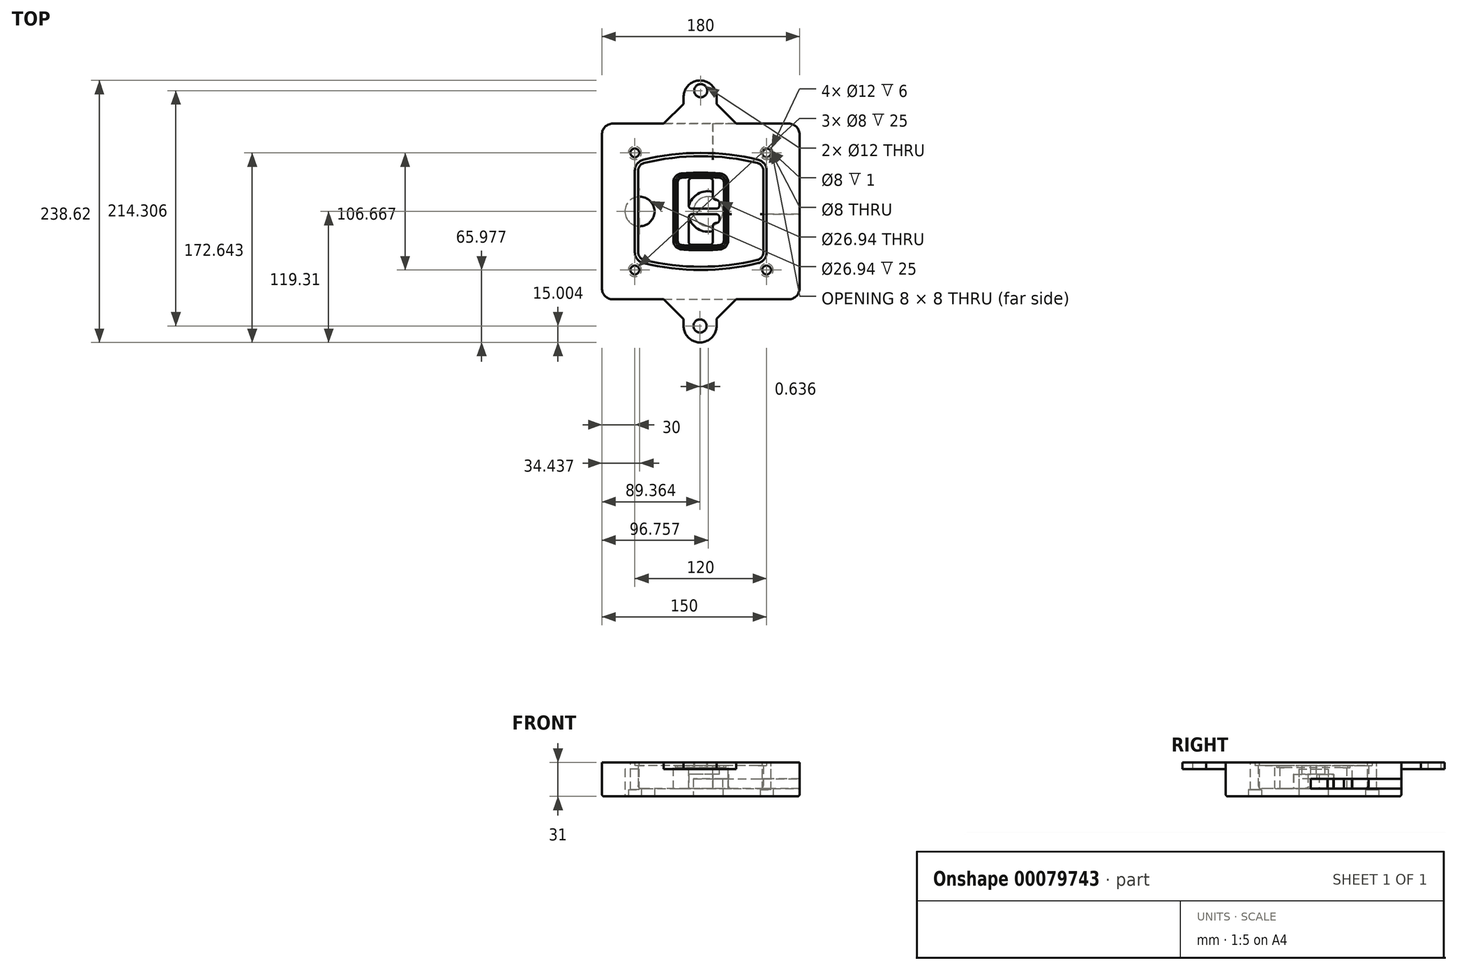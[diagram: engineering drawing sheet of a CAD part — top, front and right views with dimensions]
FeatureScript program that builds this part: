
annotation { "Feature Type Name" : "Feature", "Feature Type Description" : "" }
export const myFeature = defineFeature(function(context is Context, id is Id, definition is map)
    precondition{}
    {
        {
            var Q0;
            Q0=qCreatedBy(makeId("Top.planeOp"),FACE);
            var sketch = newSketch(context, id + "F0", { "sketchPlane" : qUnion([Q0])});
            skPoint(sketch, "E0.rect.middle", {"position": v(0, 0) * mm});
            skLineSegment(sketch, "E1.bottom", {"start": v(-80, -80) * mm, "end": v(80, -80) * mm});
            skLineSegment(sketch, "E1.top", {"start": v(-80, 80) * mm, "end": v(80, 80) * mm});
            skLineSegment(sketch, "E1.left", {"start": v(-90, -70) * mm, "end": v(-90, 70) * mm});
            skLineSegment(sketch, "E1.right", {"start": v(90, -70) * mm, "end": v(90, 70) * mm});
            skLineSegment(sketch, "E2", {"start": v(-90, 80) * mm, "end": v(90, -80) * mm, "construction": true});
            skLineSegment(sketch, "E3", {"start": v(90, 80) * mm, "end": v(-90, -80) * mm, "construction": true});
            skCircle(sketch, "E4", {"center": v(-60, 53.33) * mm, "radius": 4 * mm});
            skCircle(sketch, "E5", {"center": v(60, 53.33) * mm, "radius": 4 * mm});
            skCircle(sketch, "E6", {"center": v(60, -53.33) * mm, "radius": 4 * mm});
            skCircle(sketch, "E7", {"center": v(-60, -53.33) * mm, "radius": 4 * mm});
            skLineSegment(sketch, "E8", {"start": v(-60, 53.33) * mm, "end": v(60, 53.33) * mm, "construction": true});
            skLineSegment(sketch, "E9", {"start": v(60, 53.33) * mm, "end": v(60, -53.33) * mm, "construction": true});
            skLineSegment(sketch, "E10", {"start": v(60, -53.33) * mm, "end": v(-60, -53.33) * mm, "construction": true});
            skLineSegment(sketch, "E11", {"start": v(-60, -53.33) * mm, "end": v(-60, 53.33) * mm, "construction": true});
            skLineSegment(sketch, "E12", {"start": v(-60, 37.3) * mm, "end": v(-60, -37.3) * mm});
            skLineSegment(sketch, "E13", {"start": v(60, 37.3) * mm, "end": v(60, -37.3) * mm});
            skArc(sketch, "E14", {"start": v(52.38, 47.01) * mm, "mid": v(0, 53.33) * mm, "end": v(-52.38, 47.01) * mm});
            skArc(sketch, "E15", {"start": v(-52.38, -47.01) * mm, "mid": v(0, -53.33) * mm, "end": v(52.38, -47.01) * mm});
            skLineSegment(sketch, "E16", {"start": v(-60, 0) * mm, "end": v(60, 0) * mm, "construction": true});
            skPoint(sketch, "E17.visualSharp", {"position": v(-60, -45) * mm});
            skArc(sketch, "E17.filletArc", {"start": v(-60, -37.3) * mm, "mid": v(-57.87, -43.47) * mm, "end": v(-52.38, -47.01) * mm});
            skPoint(sketch, "E18.visualSharp", {"position": v(-60, 45) * mm});
            skArc(sketch, "E18.filletArc", {"start": v(-52.38, 47.01) * mm, "mid": v(-57.87, 43.47) * mm, "end": v(-60, 37.3) * mm});
            skPoint(sketch, "E19.visualSharp", {"position": v(60, 45) * mm});
            skArc(sketch, "E19.filletArc", {"start": v(60, 37.3) * mm, "mid": v(57.87, 43.47) * mm, "end": v(52.38, 47.01) * mm});
            skPoint(sketch, "E20.visualSharp", {"position": v(60, -45) * mm});
            skArc(sketch, "E20.filletArc", {"start": v(52.38, -47.01) * mm, "mid": v(57.87, -43.47) * mm, "end": v(60, -37.3) * mm});
            skPoint(sketch, "E21.visualSharp", {"position": v(-90, 80) * mm});
            skArc(sketch, "E21.filletArc", {"start": v(-80, 80) * mm, "mid": v(-87.07, 77.07) * mm, "end": v(-90, 70) * mm});
            skPoint(sketch, "E22.visualSharp", {"position": v(90, 80) * mm});
            skArc(sketch, "E22.filletArc", {"start": v(90, 70) * mm, "mid": v(87.07, 77.07) * mm, "end": v(80, 80) * mm});
            skPoint(sketch, "E23.visualSharp", {"position": v(90, -80) * mm});
            skArc(sketch, "E23.filletArc", {"start": v(80, -80) * mm, "mid": v(87.07, -77.07) * mm, "end": v(90, -70) * mm});
            skPoint(sketch, "E24.visualSharp", {"position": v(-90, -80) * mm});
            skArc(sketch, "E24.filletArc", {"start": v(-90, -70) * mm, "mid": v(-87.07, -77.07) * mm, "end": v(-80, -80) * mm});
            skArc(sketch, "E25.0", {"start": v(57, 37.3) * mm, "mid": v(55.5, 41.62) * mm, "end": v(51.67, 44.1) * mm});
            skLineSegment(sketch, "E25.1", {"start": v(57, 37.3) * mm, "end": v(57, -37.3) * mm});
            skArc(sketch, "E25.2", {"start": v(51.67, -44.1) * mm, "mid": v(55.5, -41.62) * mm, "end": v(57, -37.3) * mm});
            skArc(sketch, "E25.3", {"start": v(-51.67, -44.1) * mm, "mid": v(0, -50.33) * mm, "end": v(51.67, -44.1) * mm});
            skArc(sketch, "E25.4", {"start": v(-57, -37.3) * mm, "mid": v(-55.5, -41.62) * mm, "end": v(-51.67, -44.1) * mm});
            skArc(sketch, "E25.5", {"start": v(51.67, 44.1) * mm, "mid": v(0, 50.33) * mm, "end": v(-51.67, 44.1) * mm});
            skLineSegment(sketch, "E25.6", {"start": v(-57, 37.3) * mm, "end": v(-57, -37.3) * mm});
            skArc(sketch, "E25.7", {"start": v(-51.67, 44.1) * mm, "mid": v(-55.5, 41.62) * mm, "end": v(-57, 37.3) * mm});
            skArc(sketch, "E26.0", {"start": v(-53.33, 50.9) * mm, "mid": v(-61.01, 45.94) * mm, "end": v(-64, 37.3) * mm});
            skArc(sketch, "E26.1", {"start": v(53.33, 50.9) * mm, "mid": v(0, 57.33) * mm, "end": v(-53.33, 50.9) * mm});
            skArc(sketch, "E26.2", {"start": v(64, 37.3) * mm, "mid": v(61.01, 45.94) * mm, "end": v(53.33, 50.9) * mm});
            skLineSegment(sketch, "E26.3", {"start": v(64, 37.3) * mm, "end": v(64, -37.3) * mm});
            skArc(sketch, "E26.4", {"start": v(53.33, -50.9) * mm, "mid": v(61.01, -45.94) * mm, "end": v(64, -37.3) * mm});
            skLineSegment(sketch, "E26.5", {"start": v(-64, 37.3) * mm, "end": v(-64, -37.3) * mm});
            skArc(sketch, "E26.6", {"start": v(-53.33, -50.9) * mm, "mid": v(0, -57.33) * mm, "end": v(53.33, -50.9) * mm});
            skArc(sketch, "E26.7", {"start": v(-64, -37.3) * mm, "mid": v(-61.01, -45.94) * mm, "end": v(-53.33, -50.9) * mm});
            skSolve(sketch);
        }
        {
            var Q0;
            Q0=makeQuery(id+"F0.imprint","IMPRINT",FACE,{"disambiguationData":[TD([[makeQuery(id+"F0.imprint","IMPRINT",EDGE,{"derivedFrom":sQuery(id+"F0.wireOp",EDGE,"E1.bottom")}),1.0]])]});
            var Q1;
            Q1=makeQuery(id+"F0.imprint","IMPRINT",FACE,{"disambiguationData":[TD([[makeQuery(id+"F0.imprint","IMPRINT",EDGE,{"derivedFrom":sQuery(id+"F0.wireOp",EDGE,"E12")}),1.0]])]});
            var Q2;
            Q2=makeQuery(id+"F0.imprint","IMPRINT",FACE,{"disambiguationData":[TD([[makeQuery(id+"F0.imprint","IMPRINT",EDGE,{"derivedFrom":sQuery(id+"F0.wireOp",EDGE,"E25.0")}),1.0]])]});
            var Q3;
            Q3=makeQuery(id+"F0.imprint","IMPRINT",FACE,{"disambiguationData":[TD([[makeQuery(id+"F0.imprint","IMPRINT",EDGE,{"derivedFrom":sQuery(id+"F0.wireOp",EDGE,"E12")}),-1.0]])]});
            extrude(context, id + "F1", {"entities" : qUnion([Q0, Q1, Q2, Q3]), "oppositeDirection" : true, "depth" : 25 * mm});
        }
        {
            var Q0;
            Q0=makeQuery(id+"F0.imprint","IMPRINT",FACE,{"disambiguationData":[TD([[makeQuery(id+"F0.imprint","IMPRINT",EDGE,{"derivedFrom":sQuery(id+"F0.wireOp",EDGE,"E12")}),1.0]])]});
            extrude(context, id + "F2", {"entities" : qUnion([Q0]), "operationType" : NewBodyOperationType.ADD, "depth" : 3 * mm});
        }
        {
            var Q0;
            Q0=makeQuery(id+"F0.imprint","IMPRINT",FACE,{"disambiguationData":[TD([[makeQuery(id+"F0.imprint","IMPRINT",EDGE,{"derivedFrom":sQuery(id+"F0.wireOp",EDGE,"E25.0")}),1.0]])]});
            extrude(context, id + "F3", {"entities" : qUnion([Q0]), "operationType" : NewBodyOperationType.REMOVE, "oppositeDirection" : true, "depth" : 18 * mm});
        }
        {
            var Q0;
            Q0=makeQuery(id+"F2.opExtrude","CAP_FACE",FACE,{"disambiguationData":[OSD([sQuery(id+"F0.wireOp",EDGE,"E12"),sQuery(id+"F0.wireOp",EDGE,"E13"),sQuery(id+"F0.wireOp",EDGE,"E14"),sQuery(id+"F0.wireOp",EDGE,"E15"),sQuery(id+"F0.wireOp",EDGE,"E17.filletArc"),sQuery(id+"F0.wireOp",EDGE,"E18.filletArc"),sQuery(id+"F0.wireOp",EDGE,"E19.filletArc"),sQuery(id+"F0.wireOp",EDGE,"E20.filletArc"),sQuery(id+"F0.wireOp",EDGE,"E25.0"),sQuery(id+"F0.wireOp",EDGE,"E25.1"),sQuery(id+"F0.wireOp",EDGE,"E25.2"),sQuery(id+"F0.wireOp",EDGE,"E25.3"),sQuery(id+"F0.wireOp",EDGE,"E25.4"),sQuery(id+"F0.wireOp",EDGE,"E25.5"),sQuery(id+"F0.wireOp",EDGE,"E25.6"),sQuery(id+"F0.wireOp",EDGE,"E25.7")])],"isStart":false});
            var sketch = newSketch(context, id + "F4", { "sketchPlane" : qUnion([Q0])});
            skArc(sketch, "E27.0", {"start": v(-17.7, -34.56) * mm, "mid": v(0, -35.33) * mm, "end": v(17.7, -34.56) * mm});
            skArc(sketch, "E28.0", {"start": v(17.7, 34.56) * mm, "mid": v(0, 35.33) * mm, "end": v(-17.7, 34.56) * mm});
            skLineSegment(sketch, "E29", {"start": v(-25, 26.59) * mm, "end": v(-25, -26.59) * mm});
            skLineSegment(sketch, "E30", {"start": v(25, 26.59) * mm, "end": v(25, -26.59) * mm});
            skLineSegment(sketch, "E31", {"start": v(-25, 33.78) * mm, "end": v(25, 33.78) * mm, "construction": true});
            skLineSegment(sketch, "E32", {"start": v(-25, -33.78) * mm, "end": v(25, -33.78) * mm, "construction": true});
            skPoint(sketch, "E33.visualSharp", {"position": v(-25, 33.78) * mm});
            skArc(sketch, "E33.filletArc", {"start": v(-17.7, 34.56) * mm, "mid": v(-22.9, 32) * mm, "end": v(-25, 26.59) * mm});
            skPoint(sketch, "E34.visualSharp", {"position": v(25, 33.78) * mm});
            skArc(sketch, "E34.filletArc", {"start": v(25, 26.59) * mm, "mid": v(22.9, 32) * mm, "end": v(17.7, 34.56) * mm});
            skPoint(sketch, "E35.visualSharp", {"position": v(25, -33.78) * mm});
            skArc(sketch, "E35.filletArc", {"start": v(17.7, -34.56) * mm, "mid": v(22.9, -32) * mm, "end": v(25, -26.59) * mm});
            skPoint(sketch, "E36.visualSharp", {"position": v(-25, -33.78) * mm});
            skArc(sketch, "E36.filletArc", {"start": v(-25, -26.59) * mm, "mid": v(-22.9, -32) * mm, "end": v(-17.7, -34.56) * mm});
            skArc(sketch, "E37.0", {"start": v(51.67, 44.1) * mm, "mid": v(0, 50.33) * mm, "end": v(-51.67, 44.1) * mm});
            skArc(sketch, "E37.1", {"start": v(-51.67, 44.1) * mm, "mid": v(-55.5, 41.62) * mm, "end": v(-57, 37.3) * mm});
            skLineSegment(sketch, "E37.2", {"start": v(-57, 37.3) * mm, "end": v(-57, -37.3) * mm});
            skArc(sketch, "E37.3", {"start": v(-57, -37.3) * mm, "mid": v(-55.5, -41.62) * mm, "end": v(-51.67, -44.1) * mm});
            skArc(sketch, "E37.4", {"start": v(-51.67, -44.1) * mm, "mid": v(0, -50.33) * mm, "end": v(51.67, -44.1) * mm});
            skArc(sketch, "E37.5", {"start": v(51.67, -44.1) * mm, "mid": v(55.5, -41.62) * mm, "end": v(57, -37.3) * mm});
            skLineSegment(sketch, "E37.6", {"start": v(57, 37.3) * mm, "end": v(57, -37.3) * mm});
            skArc(sketch, "E37.7", {"start": v(57, 37.3) * mm, "mid": v(55.5, 41.62) * mm, "end": v(51.67, 44.1) * mm});
            skLineSegment(sketch, "E38.0", {"start": v(23, 26.59) * mm, "end": v(23, -26.59) * mm});
            skArc(sketch, "E38.1", {"start": v(17.53, -32.56) * mm, "mid": v(21.42, -30.64) * mm, "end": v(23, -26.59) * mm});
            skArc(sketch, "E38.2", {"start": v(-17.53, -32.56) * mm, "mid": v(0, -33.33) * mm, "end": v(17.53, -32.56) * mm});
            skArc(sketch, "E38.3", {"start": v(-23, -26.59) * mm, "mid": v(-21.42, -30.64) * mm, "end": v(-17.53, -32.56) * mm});
            skLineSegment(sketch, "E38.4", {"start": v(-23, 26.59) * mm, "end": v(-23, -26.59) * mm});
            skArc(sketch, "E38.5", {"start": v(23, 26.59) * mm, "mid": v(21.42, 30.64) * mm, "end": v(17.53, 32.56) * mm});
            skArc(sketch, "E38.6", {"start": v(-17.53, 32.56) * mm, "mid": v(-21.42, 30.64) * mm, "end": v(-23, 26.59) * mm});
            skArc(sketch, "E38.7", {"start": v(17.53, 32.56) * mm, "mid": v(0, 33.33) * mm, "end": v(-17.53, 32.56) * mm});
            skArc(sketch, "E39.0", {"start": v(21, 26.59) * mm, "mid": v(19.95, 29.29) * mm, "end": v(17.35, 30.57) * mm});
            skLineSegment(sketch, "E39.1", {"start": v(21, 26.59) * mm, "end": v(21, -26.59) * mm});
            skArc(sketch, "E39.2", {"start": v(17.35, -30.57) * mm, "mid": v(19.95, -29.29) * mm, "end": v(21, -26.59) * mm});
            skArc(sketch, "E39.3", {"start": v(-17.35, -30.57) * mm, "mid": v(0, -31.33) * mm, "end": v(17.35, -30.57) * mm});
            skArc(sketch, "E39.4", {"start": v(-21, -26.59) * mm, "mid": v(-19.95, -29.29) * mm, "end": v(-17.35, -30.57) * mm});
            skArc(sketch, "E39.5", {"start": v(17.35, 30.57) * mm, "mid": v(0, 31.33) * mm, "end": v(-17.35, 30.57) * mm});
            skLineSegment(sketch, "E39.6", {"start": v(-21, 26.59) * mm, "end": v(-21, -26.59) * mm});
            skArc(sketch, "E39.7", {"start": v(-17.35, 30.57) * mm, "mid": v(-19.95, 29.29) * mm, "end": v(-21, 26.59) * mm});
            skLineSegment(sketch, "E40", {"start": v(-25, 0) * mm, "end": v(25, 0) * mm, "construction": true});
            skLineSegment(sketch, "E41", {"start": v(-11, 5.5) * mm, "end": v(-11, 27.5) * mm});
            skLineSegment(sketch, "E42", {"start": v(-8, 30.5) * mm, "end": v(8, 30.5) * mm});
            skLineSegment(sketch, "E43", {"start": v(11, 27.5) * mm, "end": v(11, 13.5) * mm});
            skLineSegment(sketch, "E44", {"start": v(14, 10.5) * mm, "end": v(14, 10.5) * mm});
            skLineSegment(sketch, "E45", {"start": v(17, 7.5) * mm, "end": v(17, 5.5) * mm});
            skLineSegment(sketch, "E46", {"start": v(14, 2.5) * mm, "end": v(-8, 2.5) * mm});
            skPoint(sketch, "E47.visualSharp", {"position": v(-11, 30.5) * mm});
            skArc(sketch, "E47.filletArc", {"start": v(-8, 30.5) * mm, "mid": v(-10.12, 29.62) * mm, "end": v(-11, 27.5) * mm});
            skPoint(sketch, "E48.visualSharp", {"position": v(11, 30.5) * mm});
            skArc(sketch, "E48.filletArc", {"start": v(11, 27.5) * mm, "mid": v(10.12, 29.62) * mm, "end": v(8, 30.5) * mm});
            skPoint(sketch, "E49.visualSharp", {"position": v(11, 10.5) * mm});
            skArc(sketch, "E49.filletArc", {"start": v(11, 13.5) * mm, "mid": v(11.88, 11.38) * mm, "end": v(14, 10.5) * mm});
            skPoint(sketch, "E50.visualSharp", {"position": v(17, 10.5) * mm});
            skArc(sketch, "E50.filletArc", {"start": v(17, 7.5) * mm, "mid": v(16.12, 9.62) * mm, "end": v(14, 10.5) * mm});
            skPoint(sketch, "E51.visualSharp", {"position": v(17, 2.5) * mm});
            skArc(sketch, "E51.filletArc", {"start": v(14, 2.5) * mm, "mid": v(16.12, 3.38) * mm, "end": v(17, 5.5) * mm});
            skPoint(sketch, "E52.visualSharp", {"position": v(-11, 2.5) * mm});
            skArc(sketch, "E52.filletArc", {"start": v(-11, 5.5) * mm, "mid": v(-10.12, 3.38) * mm, "end": v(-8, 2.5) * mm});
            skLineSegment(sketch, "E53.0.MirrorCS", {"start": v(14, -2.5) * mm, "end": v(-8, -2.5) * mm});
            skArc(sketch, "E54.0.MirrorCS", {"start": v(-11, -5.5) * mm, "mid": v(-10.12, -3.38) * mm, "end": v(-8, -2.5) * mm});
            skLineSegment(sketch, "E55.0.MirrorCS", {"start": v(-11, -5.5) * mm, "end": v(-11, -27.5) * mm});
            skArc(sketch, "E56.0.MirrorCS", {"start": v(-8, -30.5) * mm, "mid": v(-10.12, -29.62) * mm, "end": v(-11, -27.5) * mm});
            skLineSegment(sketch, "E57.0.MirrorCS", {"start": v(-8, -30.5) * mm, "end": v(8, -30.5) * mm});
            skArc(sketch, "E58.0.MirrorCS", {"start": v(11, -27.5) * mm, "mid": v(10.12, -29.62) * mm, "end": v(8, -30.5) * mm});
            skLineSegment(sketch, "E59.0.MirrorCS", {"start": v(11, -27.5) * mm, "end": v(11, -13.5) * mm});
            skArc(sketch, "E60.0.MirrorCS", {"start": v(11, -13.5) * mm, "mid": v(11.88, -11.38) * mm, "end": v(14, -10.5) * mm});
            skArc(sketch, "E61.0.MirrorCS", {"start": v(17, -7.5) * mm, "mid": v(16.12, -9.62) * mm, "end": v(14, -10.5) * mm});
            skLineSegment(sketch, "E62.0.MirrorCS", {"start": v(17, -7.5) * mm, "end": v(17, -5.5) * mm});
            skArc(sketch, "E63.0.MirrorCS", {"start": v(14, -2.5) * mm, "mid": v(16.12, -3.38) * mm, "end": v(17, -5.5) * mm});
            skSolve(sketch);
        }
        {
            var Q0;
            Q0=makeQuery(id+"F4.imprint","IMPRINT",FACE,{"disambiguationData":[TD([[makeQuery(id+"F4.imprint","IMPRINT",EDGE,{"derivedFrom":sQuery(id+"F4.wireOp",EDGE,"E27.0")}),1.0]])]});
            var Q1;
            Q1=makeQuery(id+"F4.imprint","IMPRINT",FACE,{"disambiguationData":[TD([[makeQuery(id+"F4.imprint","IMPRINT",EDGE,{"derivedFrom":sQuery(id+"F4.wireOp",EDGE,"E38.0")}),-1.0]])]});
            var Q2;
            Q2=makeQuery(id+"F4.imprint","IMPRINT",FACE,{"disambiguationData":[TD([[makeQuery(id+"F4.imprint","IMPRINT",EDGE,{"derivedFrom":sQuery(id+"F4.wireOp",EDGE,"E39.0")}),1.0]])]});
            extrude(context, id + "F5", {"entities" : qUnion([Q0, Q1, Q2]), "operationType" : NewBodyOperationType.ADD, "endBound" : BoundingType.UP_TO_NEXT, "oppositeDirection" : true, "depth" : 25 * mm});
        }
        {
            var Q0;
            Q0=makeQuery(id+"F4.imprint","IMPRINT",FACE,{"disambiguationData":[TD([[makeQuery(id+"F4.imprint","IMPRINT",EDGE,{"derivedFrom":sQuery(id+"F4.wireOp",EDGE,"E38.0")}),-1.0]])]});
            extrude(context, id + "F6", {"entities" : qUnion([Q0]), "operationType" : NewBodyOperationType.REMOVE, "oppositeDirection" : true, "depth" : 2 * mm});
        }
        {
            var Q0;
            Q0=makeQuery(id+"F1.opExtrude","CAP_FACE",FACE,{"disambiguationData":[OSD([sQuery(id+"F0.wireOp",EDGE,"E1.bottom"),sQuery(id+"F0.wireOp",EDGE,"E1.top"),sQuery(id+"F0.wireOp",EDGE,"E1.left"),sQuery(id+"F0.wireOp",EDGE,"E1.right"),sQuery(id+"F0.wireOp",EDGE,"E4"),sQuery(id+"F0.wireOp",EDGE,"E5"),sQuery(id+"F0.wireOp",EDGE,"E6"),sQuery(id+"F0.wireOp",EDGE,"E7"),sQuery(id+"F0.wireOp",EDGE,"E21.filletArc"),sQuery(id+"F0.wireOp",EDGE,"E22.filletArc"),sQuery(id+"F0.wireOp",EDGE,"E23.filletArc"),sQuery(id+"F0.wireOp",EDGE,"E24.filletArc")])],"isStart":false});
            var sketch = newSketch(context, id + "F7", { "sketchPlane" : qUnion([Q0])});
            skCircle(sketch, "E64", {"center": v(6.76, 0) * mm, "radius": 13.47 * mm});
            skCircle(sketch, "E65", {"center": v(-55.56, 0) * mm, "radius": 13.47 * mm});
            skLineSegment(sketch, "E66", {"start": v(90, 0) * mm, "end": v(-90, 0) * mm});
            skCircle(sketch, "E67", {"center": v(6.76, 0) * mm, "radius": 18.47 * mm});
            skCircle(sketch, "E68", {"center": v(60, -53.33) * mm, "radius": 6 * mm});
            skCircle(sketch, "E69", {"center": v(-60, -53.33) * mm, "radius": 6 * mm});
            skCircle(sketch, "E70", {"center": v(-60, 53.33) * mm, "radius": 6 * mm});
            skCircle(sketch, "E71", {"center": v(60, 53.33) * mm, "radius": 6 * mm});
            skSolve(sketch);
        }
        {
            var Q0;
            {var subQ1=sQuery(id+"F7.wireOp",EDGE,"E66");var subQ4=sQuery(id+"F7.wireOp",EDGE,"E64");var subQ6=makeQuery(id+"F7.imprint","INTERSECT",VERTEX,{"disambiguationData":[OD(0.0)],"derivedFrom":[subQ4,subQ1]});Q0=makeQuery(id+"F7.imprint","IMPRINT",FACE,{"disambiguationData":[TD([[makeQuery(id+"F7.imprint","IMPRINT",EDGE,{"disambiguationData":[TD([[subQ6,-1.0]])],"derivedFrom":subQ4}),-1.0]])]});}
            var Q1;
            {var subQ0=sQuery(id+"F7.wireOp",EDGE,"E66");var subQ1=sQuery(id+"F7.wireOp",EDGE,"E64");var subQ3=makeQuery(id+"F7.imprint","INTERSECT",VERTEX,{"disambiguationData":[OD(0.0)],"derivedFrom":[subQ1,subQ0]});Q1=makeQuery(id+"F7.imprint","IMPRINT",FACE,{"disambiguationData":[TD([[makeQuery(id+"F7.imprint","IMPRINT",EDGE,{"disambiguationData":[TD([[subQ3,-1.0]])],"derivedFrom":subQ1}),1.0]])]});}
            var Q2;
            {var subQ0=sQuery(id+"F7.wireOp",EDGE,"E66");var subQ1=sQuery(id+"F7.wireOp",EDGE,"E64");var subQ3=makeQuery(id+"F7.imprint","INTERSECT",VERTEX,{"disambiguationData":[OD(0.0)],"derivedFrom":[subQ1,subQ0]});Q2=makeQuery(id+"F7.imprint","IMPRINT",FACE,{"disambiguationData":[TD([[makeQuery(id+"F7.imprint","IMPRINT",EDGE,{"disambiguationData":[TD([[subQ3,1.0]])],"derivedFrom":subQ1}),1.0]])]});}
            var Q3;
            {var subQ1=sQuery(id+"F7.wireOp",EDGE,"E66");var subQ4=sQuery(id+"F7.wireOp",EDGE,"E64");var subQ6=makeQuery(id+"F7.imprint","INTERSECT",VERTEX,{"disambiguationData":[OD(0.0)],"derivedFrom":[subQ4,subQ1]});Q3=makeQuery(id+"F7.imprint","IMPRINT",FACE,{"disambiguationData":[TD([[makeQuery(id+"F7.imprint","IMPRINT",EDGE,{"disambiguationData":[TD([[subQ6,1.0]])],"derivedFrom":subQ4}),-1.0]])]});}
            extrude(context, id + "F8", {"entities" : qUnion([Q0, Q1, Q2, Q3]), "operationType" : NewBodyOperationType.ADD, "oppositeDirection" : true, "depth" : 20 * mm});
        }
        {
            var Q0;
            {var subQ0=sQuery(id+"F7.wireOp",EDGE,"E66");var subQ1=sQuery(id+"F7.wireOp",EDGE,"E64");var subQ3=makeQuery(id+"F7.imprint","INTERSECT",VERTEX,{"disambiguationData":[OD(0.0)],"derivedFrom":[subQ1,subQ0]});Q0=makeQuery(id+"F7.imprint","IMPRINT",FACE,{"disambiguationData":[TD([[makeQuery(id+"F7.imprint","IMPRINT",EDGE,{"disambiguationData":[TD([[subQ3,-1.0]])],"derivedFrom":subQ1}),1.0]])]});}
            var Q1;
            {var subQ0=sQuery(id+"F7.wireOp",EDGE,"E66");var subQ1=sQuery(id+"F7.wireOp",EDGE,"E64");var subQ3=makeQuery(id+"F7.imprint","INTERSECT",VERTEX,{"disambiguationData":[OD(0.0)],"derivedFrom":[subQ1,subQ0]});Q1=makeQuery(id+"F7.imprint","IMPRINT",FACE,{"disambiguationData":[TD([[makeQuery(id+"F7.imprint","IMPRINT",EDGE,{"disambiguationData":[TD([[subQ3,1.0]])],"derivedFrom":subQ1}),1.0]])]});}
            extrude(context, id + "F9", {"entities" : qUnion([Q0, Q1]), "operationType" : NewBodyOperationType.REMOVE, "oppositeDirection" : true, "depth" : 16 * mm});
        }
        {
            var Q0;
            {var subQ0=sQuery(id+"F7.wireOp",EDGE,"E66");var subQ1=sQuery(id+"F7.wireOp",EDGE,"E65");var subQ3=makeQuery(id+"F7.imprint","INTERSECT",VERTEX,{"disambiguationData":[OD(0.0)],"derivedFrom":[subQ1,subQ0]});Q0=makeQuery(id+"F7.imprint","IMPRINT",FACE,{"disambiguationData":[TD([[makeQuery(id+"F7.imprint","IMPRINT",EDGE,{"disambiguationData":[TD([[subQ3,-1.0]])],"derivedFrom":subQ1}),1.0]])]});}
            var Q1;
            {var subQ0=sQuery(id+"F7.wireOp",EDGE,"E66");var subQ1=sQuery(id+"F7.wireOp",EDGE,"E65");var subQ3=makeQuery(id+"F7.imprint","INTERSECT",VERTEX,{"disambiguationData":[OD(0.0)],"derivedFrom":[subQ1,subQ0]});Q1=makeQuery(id+"F7.imprint","IMPRINT",FACE,{"disambiguationData":[TD([[makeQuery(id+"F7.imprint","IMPRINT",EDGE,{"disambiguationData":[TD([[subQ3,1.0]])],"derivedFrom":subQ1}),1.0]])]});}
            extrude(context, id + "F10", {"entities" : qUnion([Q0, Q1]), "operationType" : NewBodyOperationType.REMOVE, "oppositeDirection" : true, "depth" : 25 * mm});
        }
        {
            var Q0;
            Q0=makeQuery(id+"F7.imprint","IMPRINT",FACE,{"disambiguationData":[TD([[makeQuery(id+"F7.imprint","IMPRINT",EDGE,{"derivedFrom":sQuery(id+"F7.wireOp",EDGE,"E68")}),1.0]])]});
            var Q1;
            Q1=makeQuery(id+"F7.imprint","IMPRINT",FACE,{"disambiguationData":[TD([[makeQuery(id+"F7.imprint","IMPRINT",EDGE,{"derivedFrom":makeQuery(id+"F1.opExtrude","CAP_EDGE",EDGE,{"disambiguationData":[OSD([sQuery(id+"F0.wireOp",EDGE,"E5")])],"isStart":false})}),-1.0]])]});
            var Q2;
            Q2=makeQuery(id+"F7.imprint","IMPRINT",FACE,{"disambiguationData":[TD([[makeQuery(id+"F7.imprint","IMPRINT",EDGE,{"derivedFrom":sQuery(id+"F7.wireOp",EDGE,"E69")}),1.0]])]});
            var Q3;
            Q3=makeQuery(id+"F7.imprint","IMPRINT",FACE,{"disambiguationData":[TD([[makeQuery(id+"F7.imprint","IMPRINT",EDGE,{"derivedFrom":makeQuery(id+"F1.opExtrude","CAP_EDGE",EDGE,{"disambiguationData":[OSD([sQuery(id+"F0.wireOp",EDGE,"E4")])],"isStart":false})}),-1.0]])]});
            var Q4;
            Q4=makeQuery(id+"F7.imprint","IMPRINT",FACE,{"disambiguationData":[TD([[makeQuery(id+"F7.imprint","IMPRINT",EDGE,{"derivedFrom":sQuery(id+"F7.wireOp",EDGE,"E70")}),1.0]])]});
            var Q5;
            Q5=makeQuery(id+"F7.imprint","IMPRINT",FACE,{"disambiguationData":[TD([[makeQuery(id+"F7.imprint","IMPRINT",EDGE,{"derivedFrom":makeQuery(id+"F1.opExtrude","CAP_EDGE",EDGE,{"disambiguationData":[OSD([sQuery(id+"F0.wireOp",EDGE,"E7")])],"isStart":false})}),-1.0]])]});
            var Q6;
            Q6=makeQuery(id+"F7.imprint","IMPRINT",FACE,{"disambiguationData":[TD([[makeQuery(id+"F7.imprint","IMPRINT",EDGE,{"derivedFrom":sQuery(id+"F7.wireOp",EDGE,"E71")}),1.0]])]});
            var Q7;
            Q7=makeQuery(id+"F7.imprint","IMPRINT",FACE,{"disambiguationData":[TD([[makeQuery(id+"F7.imprint","IMPRINT",EDGE,{"derivedFrom":makeQuery(id+"F1.opExtrude","CAP_EDGE",EDGE,{"disambiguationData":[OSD([sQuery(id+"F0.wireOp",EDGE,"E6")])],"isStart":false})}),-1.0]])]});
            extrude(context, id + "F11", {"entities" : qUnion([Q0, Q1, Q2, Q3, Q4, Q5, Q6, Q7]), "operationType" : NewBodyOperationType.REMOVE, "oppositeDirection" : true, "depth" : 6 * mm});
        }
        {
            var Q0;
            Q0=makeQuery(id+"F9.boolean.opBoolean","COPY",FACE,{"derivedFrom":makeQuery(id+"F9.opExtrude","CAP_FACE",FACE,{"disambiguationData":[OSD([sQuery(id+"F7.wireOp",EDGE,"E64")])],"isStart":false})});
            var sketch = newSketch(context, id + "F12", { "sketchPlane" : qUnion([Q0])});
            skArc(sketch, "E72.0", {"start": v(11, -88.19) * mm, "mid": v(97.1, -83.6) * mm, "end": v(92.5, 2.5) * mm});
            skLineSegment(sketch, "E72.1", {"start": v(11, -17.97) * mm, "end": v(11, -17.97) * mm});
            skLineSegment(sketch, "E73", {"start": v(92.5, -105.13) * mm, "end": v(102.3, -105.13) * mm});
            skLineSegment(sketch, "E74.0", {"start": v(92.5, 2.5) * mm, "end": v(14, 2.5) * mm});
            skArc(sketch, "E74.1", {"start": v(14, 2.5) * mm, "mid": v(16.12, 3.38) * mm, "end": v(17, 5.5) * mm});
            skLineSegment(sketch, "E74.2", {"start": v(17, 7.5) * mm, "end": v(17, 5.5) * mm});
            skArc(sketch, "E74.3", {"start": v(17, 7.5) * mm, "mid": v(16.12, 9.62) * mm, "end": v(14, 10.5) * mm});
            skArc(sketch, "E74.4", {"start": v(11, 13.5) * mm, "mid": v(11.88, 11.38) * mm, "end": v(14, 10.5) * mm});
            skLineSegment(sketch, "E74.5", {"start": v(11, 13.5) * mm, "end": v(11, -88.19) * mm});
            skLineSegment(sketch, "E74.7", {"start": v(92.5, -2.5) * mm, "end": v(14, -2.5) * mm});
            skArc(sketch, "E74.8", {"start": v(14, -2.5) * mm, "mid": v(16.12, -3.38) * mm, "end": v(17, -5.5) * mm});
            skLineSegment(sketch, "E74.9", {"start": v(17, -7.5) * mm, "end": v(17, -5.5) * mm});
            skArc(sketch, "E74.10", {"start": v(17, -7.5) * mm, "mid": v(16.12, -9.62) * mm, "end": v(14, -10.5) * mm});
            skArc(sketch, "E74.11", {"start": v(11, -13.5) * mm, "mid": v(11.88, -11.38) * mm, "end": v(14, -10.5) * mm});
            skLineSegment(sketch, "E74.12", {"start": v(11, -17.97) * mm, "end": v(11, -13.5) * mm});
            skPoint(sketch, "E75.orphan", {"position": v(11, -27.5) * mm});
            skPoint(sketch, "E76.orphan", {"position": v(-8, -2.5) * mm});
            skPoint(sketch, "E77.orphan", {"position": v(-8, 2.5) * mm});
            skPoint(sketch, "E78.orphan", {"position": v(11, 27.5) * mm});
            skSolve(sketch);
        }
        {
            var Q0;
            {var subQ7=sQuery(id+"F12.wireOp",EDGE,"E72.0");var subQ14=sQuery(id+"F12.wireOp",EDGE,"E72.1");var subQ16=sQuery(id+"F12.wireOp",EDGE,"E74.1");var subQ18=sQuery(id+"F12.wireOp",EDGE,"E74.8");Q0=qUnion([makeQuery(id+"F12.imprint","IMPRINT",FACE,{"disambiguationData":[TD([[makeQuery(id+"F12.imprint","IMPRINT",EDGE,{"derivedFrom":subQ7}),1.0]])]}),makeQuery(id+"F12.imprint","IMPRINT",FACE,{"disambiguationData":[TD([[makeQuery(id+"F12.imprint","IMPRINT",EDGE,{"derivedFrom":subQ14}),1.0]])]}),makeQuery(id+"F12.imprint","IMPRINT",FACE,{"disambiguationData":[TD([[makeQuery(id+"F12.imprint","IMPRINT",EDGE,{"derivedFrom":subQ16}),1.0]])]}),makeQuery(id+"F12.imprint","IMPRINT",FACE,{"disambiguationData":[TD([[makeQuery(id+"F12.imprint","IMPRINT",EDGE,{"derivedFrom":subQ18}),-1.0]])]})]);}
            var Q1;
            Q1=makeQuery(id+"F5.boolean.opBoolean","SPLIT",FACE,{"disambiguationData":[TD([makeQuery(id+"F5.opExtrude","SWEPT_FACE",FACE,{"disambiguationData":[OSD([sQuery(id+"F4.wireOp",EDGE,"E41")])]})])],"derivedFrom":makeQuery(id+"F3.boolean.opBoolean","COPY",FACE,{"derivedFrom":makeQuery(id+"F3.opExtrude","CAP_FACE",FACE,{"disambiguationData":[OSD([sQuery(id+"F0.wireOp",EDGE,"E25.0"),sQuery(id+"F0.wireOp",EDGE,"E25.1"),sQuery(id+"F0.wireOp",EDGE,"E25.2"),sQuery(id+"F0.wireOp",EDGE,"E25.3"),sQuery(id+"F0.wireOp",EDGE,"E25.4"),sQuery(id+"F0.wireOp",EDGE,"E25.5"),sQuery(id+"F0.wireOp",EDGE,"E25.6"),sQuery(id+"F0.wireOp",EDGE,"E25.7")])],"isStart":false})})});
            extrude(context, id + "F13", {"entities" : qUnion([Q0]), "operationType" : NewBodyOperationType.REMOVE, "endBound" : BoundingType.UP_TO_SURFACE, "endBoundEntityFace" : qUnion([Q1]), "depth" : 25 * mm});
        }
        {
            var Q0;
            Q0=makeQuery(id+"F3.boolean.opBoolean","COPY",EDGE,{"derivedFrom":makeQuery(id+"F3.opExtrude","CAP_EDGE",EDGE,{"disambiguationData":[OSD([sQuery(id+"F0.wireOp",EDGE,"E25.6")])],"isStart":false})});
            var Q1;
            Q1=makeQuery(id+"F8.boolean.opBoolean","INTERSECT",EDGE,{"derivedFrom":[makeQuery(id+"F5.opExtrude","SWEPT_FACE",FACE,{"disambiguationData":[OSD([sQuery(id+"F4.wireOp",EDGE,"E30")])]}),makeQuery(id+"F8.opExtrude","CAP_FACE",FACE,{"disambiguationData":[OSD([sQuery(id+"F7.wireOp",EDGE,"E67")])],"isStart":false})]});
            var Q2;
            Q2=makeQuery(id+"F8.boolean.opBoolean","INTERSECT",EDGE,{"disambiguationData":[OD(1.0)],"derivedFrom":[makeQuery(id+"F5.opExtrude","SWEPT_FACE",FACE,{"disambiguationData":[OSD([sQuery(id+"F4.wireOp",EDGE,"E30")])]}),makeQuery(id+"F8.opExtrude","SWEPT_FACE",FACE,{"disambiguationData":[OSD([sQuery(id+"F7.wireOp",EDGE,"E67")])]})]});
            var Q3;
            {var subQ0=makeQuery(id+"F3.boolean.opBoolean","COPY",FACE,{"derivedFrom":makeQuery(id+"F3.opExtrude","CAP_FACE",FACE,{"disambiguationData":[OSD([sQuery(id+"F0.wireOp",EDGE,"E25.0"),sQuery(id+"F0.wireOp",EDGE,"E25.1"),sQuery(id+"F0.wireOp",EDGE,"E25.2"),sQuery(id+"F0.wireOp",EDGE,"E25.3"),sQuery(id+"F0.wireOp",EDGE,"E25.4"),sQuery(id+"F0.wireOp",EDGE,"E25.5"),sQuery(id+"F0.wireOp",EDGE,"E25.6"),sQuery(id+"F0.wireOp",EDGE,"E25.7")])],"isStart":false})});var subQ1=sQuery(id+"F4.wireOp",EDGE,"E30");Q3=makeQuery(id+"F8.boolean.opBoolean","SPLIT",EDGE,{"disambiguationData":[TD([makeQuery(id+"F5.opExtrude","SWEPT_FACE",FACE,{"disambiguationData":[OSD([sQuery(id+"F4.wireOp",EDGE,"E35.filletArc")])]})])],"derivedFrom":makeQuery(id+"F5.opExtrude","TWEAK_EDGE",EDGE,{"derivedFrom":[subQ0,makeQuery(id+"F4.imprint","IMPRINT",EDGE,{"derivedFrom":subQ1})]})});}
            var Q4;
            {var subQ0=sQuery(id+"F0.wireOp",EDGE,"E25.0");var subQ1=sQuery(id+"F0.wireOp",EDGE,"E25.1");var subQ2=sQuery(id+"F0.wireOp",EDGE,"E25.2");var subQ3=sQuery(id+"F0.wireOp",EDGE,"E25.3");var subQ4=sQuery(id+"F0.wireOp",EDGE,"E25.4");var subQ5=sQuery(id+"F0.wireOp",EDGE,"E25.5");var subQ6=sQuery(id+"F0.wireOp",EDGE,"E25.6");var subQ7=sQuery(id+"F0.wireOp",EDGE,"E25.7");Q4=makeQuery(id+"F8.boolean.opBoolean","INTERSECT",EDGE,{"derivedFrom":[makeQuery(id+"F5.boolean.opBoolean","SPLIT",FACE,{"disambiguationData":[TD([makeQuery(id+"F2.opExtrude","SWEPT_FACE",FACE,{"disambiguationData":[OSD([subQ0])]})])],"derivedFrom":makeQuery(id+"F3.boolean.opBoolean","COPY",FACE,{"derivedFrom":makeQuery(id+"F3.opExtrude","CAP_FACE",FACE,{"disambiguationData":[OSD([subQ0,subQ1,subQ2,subQ3,subQ4,subQ5,subQ6,subQ7])],"isStart":false})})}),makeQuery(id+"F8.opExtrude","SWEPT_FACE",FACE,{"disambiguationData":[OSD([sQuery(id+"F7.wireOp",EDGE,"E67")])]})]});}
            var Q5;
            Q5=makeQuery(id+"F8.boolean.opBoolean","INTERSECT",EDGE,{"disambiguationData":[OD(0.0)],"derivedFrom":[makeQuery(id+"F5.opExtrude","SWEPT_FACE",FACE,{"disambiguationData":[OSD([sQuery(id+"F4.wireOp",EDGE,"E30")])]}),makeQuery(id+"F8.opExtrude","SWEPT_FACE",FACE,{"disambiguationData":[OSD([sQuery(id+"F7.wireOp",EDGE,"E67")])]})]});
            fillet(context, id + "F14", {"entities" : qUnion([Q0, Q1, Q2, Q3, Q4, Q5]), "radius" : 3 * mm, "tangentPropagation" : true, "allowEdgeOverflow" : false});
        }
        {
            var Q0;
            Q0=makeQuery(id+"F1.opExtrude","CAP_EDGE",EDGE,{"disambiguationData":[OSD([sQuery(id+"F0.wireOp",EDGE,"E1.bottom")])],"isStart":false});
            fillet(context, id + "F15", {"entities" : qUnion([Q0]), "radius" : 2 * mm, "tangentPropagation" : true, "allowEdgeOverflow" : false});
        }
        {
            var Q0;
            {var subQ0=sQuery(id+"F0.wireOp",EDGE,"E22.filletArc");var subQ1=sQuery(id+"F0.wireOp",EDGE,"E7");var subQ2=sQuery(id+"F0.wireOp",EDGE,"E6");var subQ3=sQuery(id+"F0.wireOp",EDGE,"E5");var subQ4=sQuery(id+"F0.wireOp",EDGE,"E4");var subQ5=sQuery(id+"F0.wireOp",EDGE,"E1.bottom");var subQ6=sQuery(id+"F0.wireOp",EDGE,"E21.filletArc");var subQ7=sQuery(id+"F0.wireOp",EDGE,"E1.top");var subQ8=sQuery(id+"F0.wireOp",EDGE,"E1.left");var subQ9=sQuery(id+"F0.wireOp",EDGE,"E1.right");var subQ10=sQuery(id+"F0.wireOp",EDGE,"E23.filletArc");var subQ11=sQuery(id+"F0.wireOp",EDGE,"E24.filletArc");Q0=makeQuery(id+"F2.boolean.opBoolean","SPLIT",FACE,{"disambiguationData":[TD([makeQuery(id+"F1.opExtrude","SWEPT_FACE",FACE,{"disambiguationData":[OSD([subQ5])]})])],"derivedFrom":makeQuery(id+"F1.opExtrude","CAP_FACE",FACE,{"disambiguationData":[OSD([subQ5,subQ7,subQ8,subQ9,subQ4,subQ3,subQ2,subQ1,subQ6,subQ0,subQ10,subQ11])],"isStart":true})});}
            var sketch = newSketch(context, id + "F16", { "sketchPlane" : qUnion([Q0])});
            skArc(sketch, "E79.0", {"start": v(-80, 80) * mm, "mid": v(-87.07, 77.07) * mm, "end": v(-90, 70) * mm});
            skLineSegment(sketch, "E79.1", {"start": v(-90, -70) * mm, "end": v(-90, 70) * mm});
            skArc(sketch, "E79.2", {"start": v(-90, -70) * mm, "mid": v(-87.07, -77.07) * mm, "end": v(-80, -80) * mm});
            skLineSegment(sketch, "E79.3", {"start": v(-80, -80) * mm, "end": v(80, -80) * mm});
            skCircle(sketch, "E79.4", {"center": v(-60, -53.33) * mm, "radius": 4 * mm});
            skArc(sketch, "E79.5", {"start": v(80, -80) * mm, "mid": v(87.07, -77.07) * mm, "end": v(90, -70) * mm});
            skLineSegment(sketch, "E79.6", {"start": v(90, -70) * mm, "end": v(90, 70) * mm});
            skCircle(sketch, "E79.7", {"center": v(60, -53.33) * mm, "radius": 4 * mm});
            skArc(sketch, "E79.8", {"start": v(90, 70) * mm, "mid": v(87.07, 77.07) * mm, "end": v(80, 80) * mm});
            skLineSegment(sketch, "E79.9", {"start": v(-80, 80) * mm, "end": v(80, 80) * mm});
            skCircle(sketch, "E79.10", {"center": v(60, 53.33) * mm, "radius": 4 * mm});
            skCircle(sketch, "E79.11", {"center": v(-60, 53.33) * mm, "radius": 4 * mm});
            skArc(sketch, "E79.12", {"start": v(52.38, 47.01) * mm, "mid": v(0, 53.33) * mm, "end": v(-52.38, 47.01) * mm});
            skArc(sketch, "E79.13", {"start": v(-52.38, 47.01) * mm, "mid": v(-57.87, 43.47) * mm, "end": v(-60, 37.3) * mm});
            skLineSegment(sketch, "E79.14", {"start": v(-60, 37.3) * mm, "end": v(-60, -37.3) * mm});
            skArc(sketch, "E79.15", {"start": v(-60, -37.3) * mm, "mid": v(-57.87, -43.47) * mm, "end": v(-52.38, -47.01) * mm});
            skArc(sketch, "E79.16", {"start": v(-52.38, -47.01) * mm, "mid": v(0, -53.33) * mm, "end": v(52.38, -47.01) * mm});
            skArc(sketch, "E79.17", {"start": v(52.38, -47.01) * mm, "mid": v(57.87, -43.47) * mm, "end": v(60, -37.3) * mm});
            skLineSegment(sketch, "E79.18", {"start": v(60, 37.3) * mm, "end": v(60, -37.3) * mm});
            skArc(sketch, "E79.19", {"start": v(60, 37.3) * mm, "mid": v(57.87, 43.47) * mm, "end": v(52.38, 47.01) * mm});
            skLineSegment(sketch, "E80", {"start": v(0, 80) * mm, "end": v(0, 110) * mm, "construction": true});
            skCircle(sketch, "E81", {"center": v(0, 110) * mm, "radius": 0.06 * mm});
            skLineSegment(sketch, "E82", {"start": v(-33.64, 80) * mm, "end": v(-15.64, 98) * mm});
            skLineSegment(sketch, "E83", {"start": v(-15.64, 98) * mm, "end": v(-15.64, 104.28) * mm});
            skLineSegment(sketch, "E84", {"start": v(32.22, 80) * mm, "end": v(14.36, 97.86) * mm});
            skLineSegment(sketch, "E85", {"start": v(14.36, 97.86) * mm, "end": v(14.36, 104.3) * mm});
            skCircle(sketch, "E86", {"center": v(0, 110) * mm, "radius": 6 * mm});
            skArc(sketch, "E87", {"start": v(14.36, 104.3) * mm, "mid": v(-0.65, 119.3) * mm, "end": v(-15.64, 104.28) * mm});
            skLineSegment(sketch, "E88", {"start": v(-90, 0) * mm, "end": v(90, 0) * mm, "construction": true});
            skLineSegment(sketch, "E89.MirrorCS", {"start": v(32.22, -80) * mm, "end": v(14.36, -97.86) * mm});
            skLineSegment(sketch, "E90.MirrorCS", {"start": v(14.36, -97.86) * mm, "end": v(14.36, -104.3) * mm});
            skLineSegment(sketch, "E91.MirrorCS", {"start": v(-15.64, -98) * mm, "end": v(-15.64, -104.28) * mm});
            skLineSegment(sketch, "E92.MirrorCS", {"start": v(-33.64, -80) * mm, "end": v(-15.64, -98) * mm});
            skArc(sketch, "E93.MirrorCS", {"start": v(14.36, -104.3) * mm, "mid": v(-0.65, -119.3) * mm, "end": v(-15.64, -104.28) * mm});
            skCircle(sketch, "E94", {"center": v(-0.64, -104.3) * mm, "radius": 6 * mm});
            skSolve(sketch);
        }
        {
            var Q0;
            Q0 = qSketchRegion(id + "F16", true);
            extrude(context, id + "F17", {"entities" : qUnion([Q0]), "operationType" : NewBodyOperationType.ADD, "depth" : 6 * mm});
        }
    });
